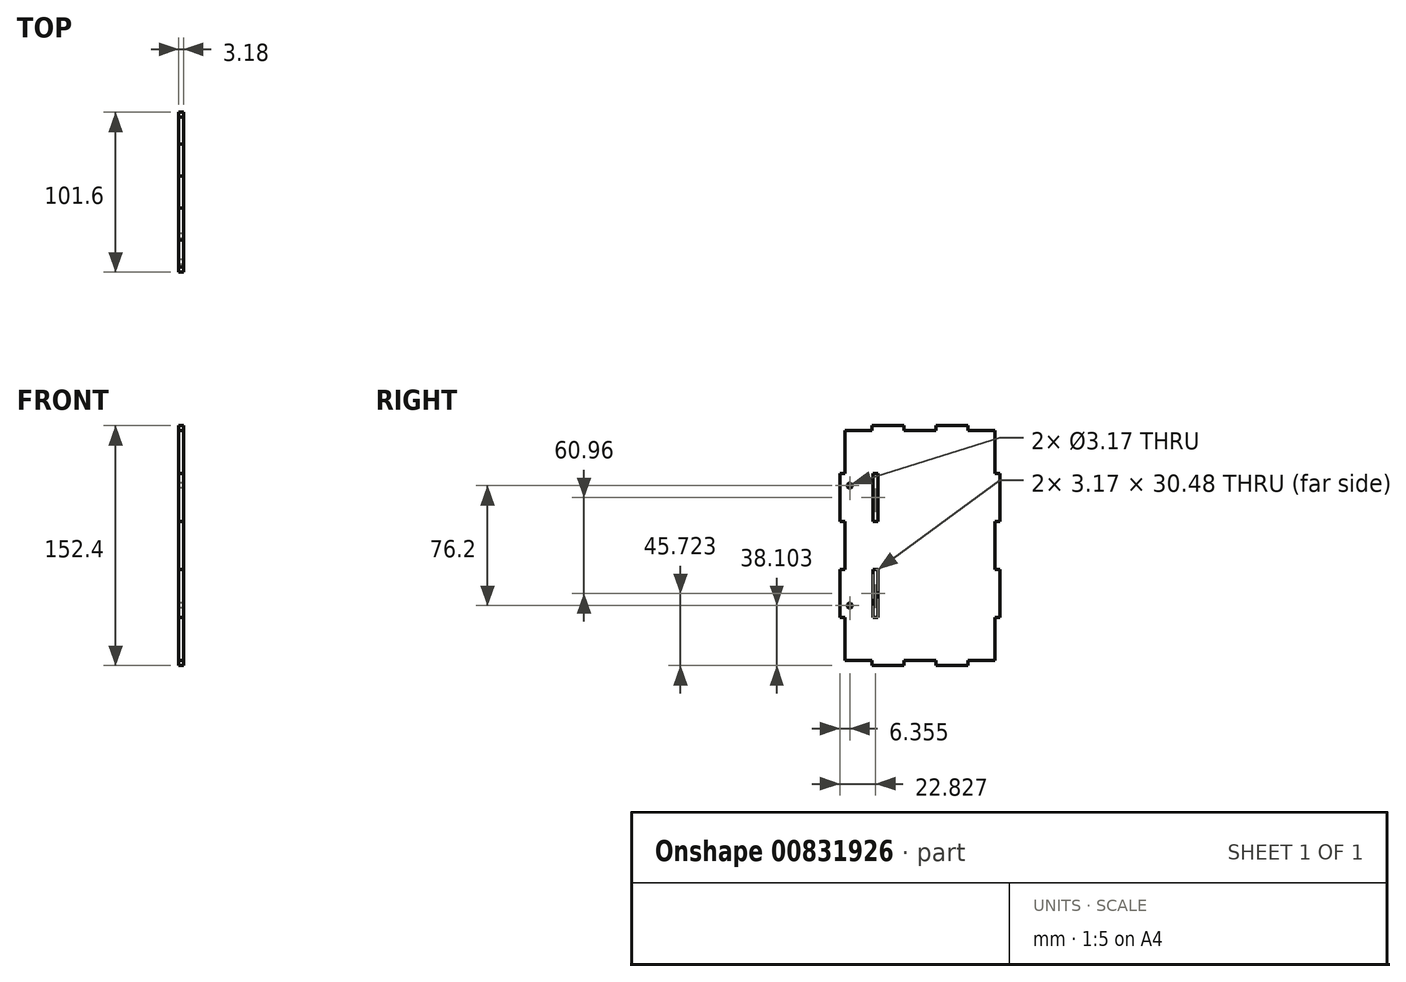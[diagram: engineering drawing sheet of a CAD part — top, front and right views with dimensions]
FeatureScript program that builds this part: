
annotation { "Feature Type Name" : "Feature", "Feature Type Description" : "" }
export const myFeature = defineFeature(function(context is Context, id is Id, definition is map)
    precondition{}
    {
        {
            var Q0;
            Q0=qCreatedBy(makeId("Right.planeOp"),FACE);
            var sketch = newSketch(context, id + "F0", { "sketchPlane" : qUnion([Q0])});
            skLineSegment(sketch, "E0", {"start": v(92.28, 99.7) * mm, "end": v(92.28, 102.88) * mm});
            skLineSegment(sketch, "E1", {"start": v(112.6, 102.88) * mm, "end": v(112.6, 99.7) * mm});
            skLineSegment(sketch, "E2", {"start": v(112.6, 99.7) * mm, "end": v(132.92, 99.7) * mm});
            skLineSegment(sketch, "E3", {"start": v(132.92, 99.7) * mm, "end": v(132.92, 102.88) * mm});
            skLineSegment(sketch, "E4", {"start": v(153.24, 102.88) * mm, "end": v(153.24, 99.7) * mm});
            skLineSegment(sketch, "E5", {"start": v(153.24, -46.34) * mm, "end": v(153.24, -49.52) * mm});
            skLineSegment(sketch, "E6", {"start": v(132.92, -49.52) * mm, "end": v(132.92, -46.34) * mm});
            skLineSegment(sketch, "E7", {"start": v(132.92, -46.34) * mm, "end": v(112.6, -46.34) * mm});
            skLineSegment(sketch, "E8", {"start": v(112.6, -46.34) * mm, "end": v(112.6, -49.52) * mm});
            skLineSegment(sketch, "E9", {"start": v(92.28, -49.52) * mm, "end": v(92.28, -46.34) * mm});
            skPoint(sketch, "E10.end.orphan", {"position": v(197.73, 99.7) * mm});
            skLineSegment(sketch, "E11", {"start": v(153.24, 99.7) * mm, "end": v(170.39, 99.7) * mm});
            skLineSegment(sketch, "E12", {"start": v(170.39, 99.7) * mm, "end": v(170.39, 72.4) * mm});
            skLineSegment(sketch, "E13", {"start": v(170.39, 72.4) * mm, "end": v(173.56, 72.4) * mm});
            skLineSegment(sketch, "E14", {"start": v(173.56, 72.4) * mm, "end": v(173.56, 41.92) * mm});
            skLineSegment(sketch, "E15", {"start": v(173.56, 41.92) * mm, "end": v(170.39, 41.92) * mm});
            skLineSegment(sketch, "E16", {"start": v(170.39, 41.92) * mm, "end": v(170.39, 11.44) * mm});
            skLineSegment(sketch, "E17", {"start": v(170.39, 11.44) * mm, "end": v(173.56, 11.44) * mm});
            skLineSegment(sketch, "E18", {"start": v(173.56, 11.44) * mm, "end": v(173.56, -19.04) * mm});
            skLineSegment(sketch, "E19", {"start": v(173.56, -19.04) * mm, "end": v(170.39, -19.04) * mm});
            skLineSegment(sketch, "E20", {"start": v(170.39, -19.04) * mm, "end": v(170.39, -46.34) * mm});
            skLineSegment(sketch, "E21", {"start": v(170.39, -46.34) * mm, "end": v(153.24, -46.34) * mm});
            skLineSegment(sketch, "E22", {"start": v(92.28, -46.34) * mm, "end": v(75.14, -46.34) * mm});
            skLineSegment(sketch, "E23", {"start": v(75.14, -46.34) * mm, "end": v(75.14, -19.04) * mm});
            skLineSegment(sketch, "E24", {"start": v(75.14, -19.04) * mm, "end": v(71.96, -19.04) * mm});
            skLineSegment(sketch, "E25", {"start": v(71.96, -19.04) * mm, "end": v(71.96, 11.44) * mm});
            skLineSegment(sketch, "E26", {"start": v(71.96, 11.44) * mm, "end": v(75.14, 11.44) * mm});
            skLineSegment(sketch, "E27", {"start": v(75.14, 11.44) * mm, "end": v(75.14, 41.92) * mm});
            skLineSegment(sketch, "E28", {"start": v(75.14, 41.92) * mm, "end": v(71.96, 41.92) * mm});
            skLineSegment(sketch, "E29", {"start": v(71.96, 41.92) * mm, "end": v(71.96, 72.4) * mm});
            skLineSegment(sketch, "E30", {"start": v(71.96, 72.4) * mm, "end": v(75.14, 72.4) * mm});
            skLineSegment(sketch, "E31", {"start": v(75.14, 72.4) * mm, "end": v(75.14, 99.7) * mm});
            skPoint(sketch, "E32.start.orphan", {"position": v(102.72, 99.7) * mm});
            skLineSegment(sketch, "E33", {"start": v(75.14, 99.7) * mm, "end": v(92.28, 99.7) * mm});
            skLineSegment(sketch, "E34", {"start": v(92.28, -49.52) * mm, "end": v(112.6, -49.52) * mm});
            skLineSegment(sketch, "E35", {"start": v(132.92, -49.52) * mm, "end": v(153.24, -49.52) * mm});
            skLineSegment(sketch, "E36", {"start": v(92.28, 102.88) * mm, "end": v(112.6, 102.88) * mm});
            skLineSegment(sketch, "E37", {"start": v(132.92, 102.88) * mm, "end": v(153.24, 102.88) * mm});
            skCircle(sketch, "E38", {"center": v(78.31, 64.78) * mm, "radius": 1.59 * mm});
            skCircle(sketch, "E39", {"center": v(78.31, -11.42) * mm, "radius": 1.59 * mm});
            skLineSegment(sketch, "E40.bottom", {"start": v(93.2, 72.4) * mm, "end": v(96.37, 72.4) * mm});
            skLineSegment(sketch, "E40.top", {"start": v(93.2, 41.92) * mm, "end": v(96.37, 41.92) * mm});
            skLineSegment(sketch, "E40.left", {"start": v(93.2, 72.4) * mm, "end": v(93.2, 41.92) * mm});
            skLineSegment(sketch, "E40.right", {"start": v(96.37, 72.4) * mm, "end": v(96.37, 41.92) * mm});
            skLineSegment(sketch, "E41.bottom", {"start": v(93.2, 11.44) * mm, "end": v(96.37, 11.44) * mm});
            skLineSegment(sketch, "E41.top", {"start": v(93.2, -19.04) * mm, "end": v(96.37, -19.04) * mm});
            skLineSegment(sketch, "E41.left", {"start": v(93.2, 11.44) * mm, "end": v(93.2, -19.04) * mm});
            skLineSegment(sketch, "E41.right", {"start": v(96.37, 11.44) * mm, "end": v(96.37, -19.04) * mm});
            skSolve(sketch);
        }
        {
            var Q0;
            Q0=makeQuery(id+"F0.imprint","IMPRINT",FACE,{"disambiguationData":[TD([[makeQuery(id+"F0.imprint","IMPRINT",EDGE,{"derivedFrom":sQuery(id+"F0.wireOp",EDGE,"E0")}),-1.0]])]});
            extrude(context, id + "F1", {"entities" : qUnion([Q0]), "depth" : 3.17 * mm, "offsetDistance" : 25.4 * mm});
        }
    });
